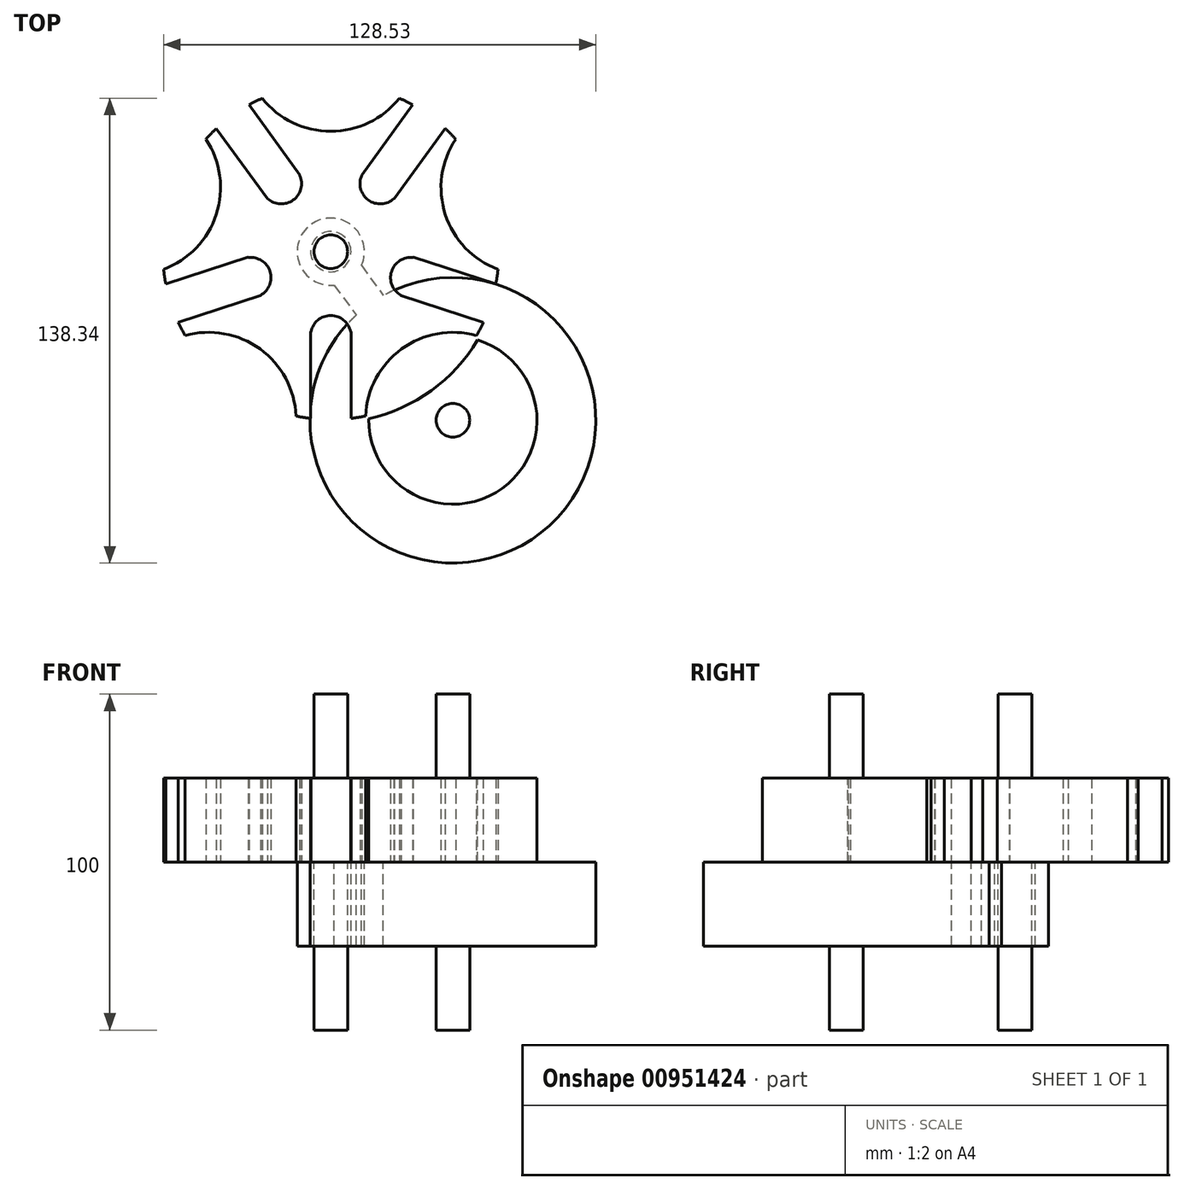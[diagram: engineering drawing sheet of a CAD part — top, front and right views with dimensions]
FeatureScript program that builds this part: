
annotation { "Feature Type Name" : "Feature", "Feature Type Description" : "" }
export const myFeature = defineFeature(function(context is Context, id is Id, definition is map)
    precondition{}
    {
        {
            var Q0;
            Q0=qCreatedBy(makeId("Top.planeOp"),FACE);
            var sketch = newSketch(context, id + "F0", { "sketchPlane" : qUnion([Q0])});
            skCircle(sketch, "E0", {"center": v(0, 0) * mm, "radius": 50 * mm});
            skCircle(sketch, "E1.cCircle", {"center": v(0, 0) * mm, "radius": 50 * mm, "construction": true});
            skLineSegment(sketch, "E1.0", {"start": v(0, -50) * mm, "end": v(-47.55, -15.45) * mm});
            skLineSegment(sketch, "E1.1", {"start": v(-47.55, -15.45) * mm, "end": v(-29.39, 40.45) * mm});
            skLineSegment(sketch, "E1.2", {"start": v(-29.39, 40.45) * mm, "end": v(29.39, 40.45) * mm});
            skLineSegment(sketch, "E1.3", {"start": v(29.39, 40.45) * mm, "end": v(47.55, -15.45) * mm});
            skLineSegment(sketch, "E1.4", {"start": v(47.55, -15.45) * mm, "end": v(0, -50) * mm});
            skLineSegment(sketch, "E2", {"start": v(-47.55, -15.45) * mm, "end": v(0, 0) * mm});
            skLineSegment(sketch, "E3", {"start": v(0, -50) * mm, "end": v(0, 0) * mm});
            skLineSegment(sketch, "E4", {"start": v(47.55, -15.45) * mm, "end": v(0, 0) * mm});
            skLineSegment(sketch, "E5", {"start": v(29.39, 40.45) * mm, "end": v(0, 0) * mm});
            skLineSegment(sketch, "E6", {"start": v(-29.39, 40.45) * mm, "end": v(0, 0) * mm});
            skLineSegment(sketch, "E7.0", {"start": v(-34.24, 36.92) * mm, "end": v(-4.85, -3.53) * mm});
            skLineSegment(sketch, "E8.0", {"start": v(-24.54, 43.98) * mm, "end": v(4.85, 3.53) * mm});
            skLineSegment(sketch, "E9.0", {"start": v(-45.7, -21.16) * mm, "end": v(1.85, -5.7) * mm});
            skLineSegment(sketch, "E10.0", {"start": v(-49.4, -9.74) * mm, "end": v(-1.85, 5.7) * mm});
            skLineSegment(sketch, "E11.0", {"start": v(-6, -50) * mm, "end": v(-6, 0) * mm});
            skLineSegment(sketch, "E12.0", {"start": v(6, -50) * mm, "end": v(6, 0) * mm});
            skLineSegment(sketch, "E13.0", {"start": v(49.4, -9.74) * mm, "end": v(1.85, 5.7) * mm});
            skLineSegment(sketch, "E14.0", {"start": v(45.7, -21.16) * mm, "end": v(-1.85, -5.7) * mm});
            skLineSegment(sketch, "E15.0", {"start": v(24.54, 43.98) * mm, "end": v(-4.85, 3.53) * mm});
            skLineSegment(sketch, "E16.0", {"start": v(34.24, 36.92) * mm, "end": v(4.85, -3.53) * mm});
            skLineSegment(sketch, "E17", {"start": v(-47.55, -15.45) * mm, "end": v(-36.33, -50) * mm});
            skLineSegment(sketch, "E18", {"start": v(0, -50) * mm, "end": v(-36.33, -50) * mm});
            skLineSegment(sketch, "E19", {"start": v(0, -50) * mm, "end": v(36.33, -50) * mm});
            skLineSegment(sketch, "E20", {"start": v(47.55, -15.45) * mm, "end": v(36.33, -50) * mm});
            skLineSegment(sketch, "E21", {"start": v(47.55, -15.45) * mm, "end": v(58.78, 19.1) * mm});
            skLineSegment(sketch, "E22", {"start": v(29.39, 40.45) * mm, "end": v(58.78, 19.1) * mm});
            skLineSegment(sketch, "E23", {"start": v(29.39, 40.45) * mm, "end": v(0, 61.8) * mm});
            skLineSegment(sketch, "E24", {"start": v(-29.39, 40.45) * mm, "end": v(0, 61.8) * mm});
            skLineSegment(sketch, "E25", {"start": v(-47.55, -15.45) * mm, "end": v(-58.78, 19.1) * mm});
            skLineSegment(sketch, "E26", {"start": v(-29.39, 40.45) * mm, "end": v(-58.78, 19.1) * mm});
            skCircle(sketch, "E27", {"center": v(36.33, -50) * mm, "radius": 36.33 * mm});
            skCircle(sketch, "E28", {"center": v(-36.33, -50) * mm, "radius": 36.33 * mm});
            skCircle(sketch, "E29", {"center": v(58.78, 19.1) * mm, "radius": 36.33 * mm});
            skCircle(sketch, "E30", {"center": v(0, 61.8) * mm, "radius": 36.33 * mm});
            skCircle(sketch, "E31", {"center": v(-58.78, 19.1) * mm, "radius": 36.33 * mm});
            skCircle(sketch, "E32", {"center": v(-6, -30) * mm, "radius": 6 * mm});
            skCircle(sketch, "E33", {"center": v(0, 0) * mm, "radius": 24.6 * mm});
            skCircle(sketch, "E34", {"center": v(0, -25) * mm, "radius": 6 * mm});
            skCircle(sketch, "E35", {"center": v(23.78, -7.73) * mm, "radius": 6 * mm});
            skCircle(sketch, "E36", {"center": v(14.7, 20.23) * mm, "radius": 6 * mm});
            skCircle(sketch, "E37", {"center": v(-14.7, 20.23) * mm, "radius": 6 * mm});
            skCircle(sketch, "E38", {"center": v(-23.78, -7.73) * mm, "radius": 6 * mm});
            skCircle(sketch, "E39", {"center": v(0, 0) * mm, "radius": 5 * mm});
            skCircle(sketch, "E40", {"center": v(36.33, -50) * mm, "radius": 26 * mm});
            skCircle(sketch, "E41", {"center": v(-36.33, -50) * mm, "radius": 26 * mm});
            skCircle(sketch, "E42", {"center": v(58.78, 19.1) * mm, "radius": 26 * mm});
            skCircle(sketch, "E43", {"center": v(0, 61.8) * mm, "radius": 26 * mm});
            skCircle(sketch, "E44", {"center": v(-58.78, 19.1) * mm, "radius": 26 * mm});
            skSolve(sketch);
        }
        {
            var Q0;
            {var subQ1=sQuery(id+"F0.wireOp",EDGE,"E1.2");var subQ7=sQuery(id+"F0.wireOp",EDGE,"E8.0");var subQ8=makeQuery(id+"F0.imprint","INTERSECT",VERTEX,{"derivedFrom":[subQ1,subQ7]});Q0=makeQuery(id+"F0.imprint","IMPRINT",FACE,{"disambiguationData":[TD([[makeQuery(id+"F0.imprint","IMPRINT",EDGE,{"disambiguationData":[TD([[subQ8,-1.0]])],"derivedFrom":subQ1}),-1.0]])]});}
            var Q1;
            {var subQ0=sQuery(id+"F0.wireOp",EDGE,"E15.0");var subQ1=sQuery(id+"F0.wireOp",EDGE,"E0");var subQ2=makeQuery(id+"F0.imprint","INTERSECT",VERTEX,{"derivedFrom":[subQ1,subQ0]});Q1=makeQuery(id+"F0.imprint","IMPRINT",FACE,{"disambiguationData":[TD([[makeQuery(id+"F0.imprint","IMPRINT",EDGE,{"disambiguationData":[TD([[subQ2,-1.0]])],"derivedFrom":subQ1}),1.0]])]});}
            var Q2;
            {var subQ0=sQuery(id+"F0.wireOp",EDGE,"E43");var subQ1=sQuery(id+"F0.wireOp",EDGE,"E0");var subQ2=makeQuery(id+"F0.imprint","INTERSECT",VERTEX,{"disambiguationData":[OD(1.0)],"derivedFrom":[subQ1,subQ0]});Q2=makeQuery(id+"F0.imprint","IMPRINT",FACE,{"disambiguationData":[TD([[makeQuery(id+"F0.imprint","IMPRINT",EDGE,{"disambiguationData":[TD([[subQ2,-1.0]])],"derivedFrom":subQ1}),1.0]])]});}
            var Q3;
            {var subQ4=sQuery(id+"F0.wireOp",EDGE,"E8.0");var subQ6=sQuery(id+"F0.wireOp",EDGE,"E30");var subQ9=makeQuery(id+"F0.imprint","INTERSECT",VERTEX,{"derivedFrom":[subQ4,subQ6]});Q3=makeQuery(id+"F0.imprint","IMPRINT",FACE,{"disambiguationData":[TD([[makeQuery(id+"F0.imprint","IMPRINT",EDGE,{"disambiguationData":[TD([[subQ9,-1.0]])],"derivedFrom":subQ4}),1.0]])]});}
            var Q4;
            {var subQ0=sQuery(id+"F0.wireOp",EDGE,"E33");var subQ1=sQuery(id+"F0.wireOp",EDGE,"E8.0");var subQ2=makeQuery(id+"F0.imprint","INTERSECT",VERTEX,{"derivedFrom":[subQ1,subQ0]});Q4=makeQuery(id+"F0.imprint","IMPRINT",FACE,{"disambiguationData":[TD([[makeQuery(id+"F0.imprint","IMPRINT",EDGE,{"disambiguationData":[TD([[subQ2,-1.0]])],"derivedFrom":subQ1}),1.0]])]});}
            var Q5;
            {var subQ3=sQuery(id+"F0.wireOp",EDGE,"E37");var subQ9=sQuery(id+"F0.wireOp",EDGE,"E6");var subQ10=makeQuery(id+"F0.imprint","INTERSECT",VERTEX,{"disambiguationData":[OD(1.0)],"derivedFrom":[subQ9,subQ3]});Q5=makeQuery(id+"F0.imprint","IMPRINT",FACE,{"disambiguationData":[TD([[makeQuery(id+"F0.imprint","IMPRINT",EDGE,{"disambiguationData":[TD([[subQ10,-1.0]])],"derivedFrom":subQ9}),1.0]])]});}
            var Q6;
            {var subQ3=sQuery(id+"F0.wireOp",EDGE,"E37");var subQ9=sQuery(id+"F0.wireOp",EDGE,"E6");var subQ10=makeQuery(id+"F0.imprint","INTERSECT",VERTEX,{"disambiguationData":[OD(1.0)],"derivedFrom":[subQ9,subQ3]});Q6=makeQuery(id+"F0.imprint","IMPRINT",FACE,{"disambiguationData":[TD([[makeQuery(id+"F0.imprint","IMPRINT",EDGE,{"disambiguationData":[TD([[subQ10,-1.0]])],"derivedFrom":subQ9}),-1.0]])]});}
            var Q7;
            {var subQ7=sQuery(id+"F0.wireOp",EDGE,"E36");var subQ9=sQuery(id+"F0.wireOp",EDGE,"E5");var subQ11=makeQuery(id+"F0.imprint","INTERSECT",VERTEX,{"disambiguationData":[OD(1.0)],"derivedFrom":[subQ9,subQ7]});Q7=makeQuery(id+"F0.imprint","IMPRINT",FACE,{"disambiguationData":[TD([[makeQuery(id+"F0.imprint","IMPRINT",EDGE,{"disambiguationData":[TD([[subQ11,-1.0]])],"derivedFrom":subQ9}),-1.0]])]});}
            var Q8;
            {var subQ3=sQuery(id+"F0.wireOp",EDGE,"E36");var subQ7=sQuery(id+"F0.wireOp",EDGE,"E5");var subQ8=makeQuery(id+"F0.imprint","INTERSECT",VERTEX,{"disambiguationData":[OD(1.0)],"derivedFrom":[subQ7,subQ3]});Q8=makeQuery(id+"F0.imprint","IMPRINT",FACE,{"disambiguationData":[TD([[makeQuery(id+"F0.imprint","IMPRINT",EDGE,{"disambiguationData":[TD([[subQ8,-1.0]])],"derivedFrom":subQ7}),1.0]])]});}
            var Q9;
            {var subQ0=sQuery(id+"F0.wireOp",EDGE,"E33");var subQ1=sQuery(id+"F0.wireOp",EDGE,"E13.0");var subQ2=makeQuery(id+"F0.imprint","INTERSECT",VERTEX,{"derivedFrom":[subQ1,subQ0]});Q9=makeQuery(id+"F0.imprint","IMPRINT",FACE,{"disambiguationData":[TD([[makeQuery(id+"F0.imprint","IMPRINT",EDGE,{"disambiguationData":[TD([[subQ2,-1.0]])],"derivedFrom":subQ1}),-1.0]])]});}
            var Q10;
            {var subQ3=sQuery(id+"F0.wireOp",EDGE,"E35");var subQ5=sQuery(id+"F0.wireOp",EDGE,"E4");var subQ6=makeQuery(id+"F0.imprint","INTERSECT",VERTEX,{"disambiguationData":[OD(1.0)],"derivedFrom":[subQ5,subQ3]});Q10=makeQuery(id+"F0.imprint","IMPRINT",FACE,{"disambiguationData":[TD([[makeQuery(id+"F0.imprint","IMPRINT",EDGE,{"disambiguationData":[TD([[subQ6,-1.0]])],"derivedFrom":subQ5}),-1.0]])]});}
            var Q11;
            {var subQ3=sQuery(id+"F0.wireOp",EDGE,"E35");var subQ9=sQuery(id+"F0.wireOp",EDGE,"E4");var subQ10=makeQuery(id+"F0.imprint","INTERSECT",VERTEX,{"disambiguationData":[OD(1.0)],"derivedFrom":[subQ9,subQ3]});Q11=makeQuery(id+"F0.imprint","IMPRINT",FACE,{"disambiguationData":[TD([[makeQuery(id+"F0.imprint","IMPRINT",EDGE,{"disambiguationData":[TD([[subQ10,-1.0]])],"derivedFrom":subQ9}),1.0]])]});}
            var Q12;
            {var subQ0=sQuery(id+"F0.wireOp",EDGE,"E33");var subQ1=sQuery(id+"F0.wireOp",EDGE,"E12.0");var subQ2=makeQuery(id+"F0.imprint","INTERSECT",VERTEX,{"derivedFrom":[subQ1,subQ0]});Q12=makeQuery(id+"F0.imprint","IMPRINT",FACE,{"disambiguationData":[TD([[makeQuery(id+"F0.imprint","IMPRINT",EDGE,{"disambiguationData":[TD([[subQ2,-1.0]])],"derivedFrom":subQ1}),-1.0]])]});}
            var Q13;
            {var subQ3=sQuery(id+"F0.wireOp",EDGE,"E34");var subQ8=sQuery(id+"F0.wireOp",EDGE,"E3");var subQ11=makeQuery(id+"F0.imprint","INTERSECT",VERTEX,{"disambiguationData":[OD(1.0)],"derivedFrom":[subQ8,subQ3]});Q13=makeQuery(id+"F0.imprint","IMPRINT",FACE,{"disambiguationData":[TD([[makeQuery(id+"F0.imprint","IMPRINT",EDGE,{"disambiguationData":[TD([[subQ11,-1.0]])],"derivedFrom":subQ8}),-1.0]])]});}
            var Q14;
            {var subQ3=sQuery(id+"F0.wireOp",EDGE,"E34");var subQ9=sQuery(id+"F0.wireOp",EDGE,"E3");var subQ10=makeQuery(id+"F0.imprint","INTERSECT",VERTEX,{"disambiguationData":[OD(1.0)],"derivedFrom":[subQ9,subQ3]});Q14=makeQuery(id+"F0.imprint","IMPRINT",FACE,{"disambiguationData":[TD([[makeQuery(id+"F0.imprint","IMPRINT",EDGE,{"disambiguationData":[TD([[subQ10,-1.0]])],"derivedFrom":subQ9}),1.0]])]});}
            var Q15;
            {var subQ0=sQuery(id+"F0.wireOp",EDGE,"E33");var subQ1=sQuery(id+"F0.wireOp",EDGE,"E9.0");var subQ2=makeQuery(id+"F0.imprint","INTERSECT",VERTEX,{"derivedFrom":[subQ1,subQ0]});Q15=makeQuery(id+"F0.imprint","IMPRINT",FACE,{"disambiguationData":[TD([[makeQuery(id+"F0.imprint","IMPRINT",EDGE,{"disambiguationData":[TD([[subQ2,-1.0]])],"derivedFrom":subQ1}),-1.0]])]});}
            var Q16;
            {var subQ7=sQuery(id+"F0.wireOp",EDGE,"E38");var subQ9=sQuery(id+"F0.wireOp",EDGE,"E2");var subQ10=makeQuery(id+"F0.imprint","INTERSECT",VERTEX,{"disambiguationData":[OD(1.0)],"derivedFrom":[subQ9,subQ7]});Q16=makeQuery(id+"F0.imprint","IMPRINT",FACE,{"disambiguationData":[TD([[makeQuery(id+"F0.imprint","IMPRINT",EDGE,{"disambiguationData":[TD([[subQ10,-1.0]])],"derivedFrom":subQ9}),-1.0]])]});}
            var Q17;
            {var subQ0=sQuery(id+"F0.wireOp",EDGE,"E33");var subQ1=sQuery(id+"F0.wireOp",EDGE,"E7.0");var subQ2=makeQuery(id+"F0.imprint","INTERSECT",VERTEX,{"derivedFrom":[subQ1,subQ0]});Q17=makeQuery(id+"F0.imprint","IMPRINT",FACE,{"disambiguationData":[TD([[makeQuery(id+"F0.imprint","IMPRINT",EDGE,{"disambiguationData":[TD([[subQ2,-1.0]])],"derivedFrom":subQ1}),-1.0]])]});}
            var Q18;
            {var subQ3=sQuery(id+"F0.wireOp",EDGE,"E38");var subQ6=sQuery(id+"F0.wireOp",EDGE,"E2");var subQ11=makeQuery(id+"F0.imprint","INTERSECT",VERTEX,{"disambiguationData":[OD(1.0)],"derivedFrom":[subQ6,subQ3]});Q18=makeQuery(id+"F0.imprint","IMPRINT",FACE,{"disambiguationData":[TD([[makeQuery(id+"F0.imprint","IMPRINT",EDGE,{"disambiguationData":[TD([[subQ11,-1.0]])],"derivedFrom":subQ6}),1.0]])]});}
            var Q19;
            {var subQ0=sQuery(id+"F0.wireOp",EDGE,"E16.0");var subQ1=sQuery(id+"F0.wireOp",EDGE,"E0");var subQ2=makeQuery(id+"F0.imprint","INTERSECT",VERTEX,{"derivedFrom":[subQ1,subQ0]});Q19=makeQuery(id+"F0.imprint","IMPRINT",FACE,{"disambiguationData":[TD([[makeQuery(id+"F0.imprint","IMPRINT",EDGE,{"disambiguationData":[TD([[subQ2,1.0]])],"derivedFrom":subQ1}),1.0]])]});}
            var Q20;
            {var subQ0=sQuery(id+"F0.wireOp",EDGE,"E16.0");var subQ1=sQuery(id+"F0.wireOp",EDGE,"E1.3");var subQ2=makeQuery(id+"F0.imprint","INTERSECT",VERTEX,{"derivedFrom":[subQ1,subQ0]});Q20=makeQuery(id+"F0.imprint","IMPRINT",FACE,{"disambiguationData":[TD([[makeQuery(id+"F0.imprint","IMPRINT",EDGE,{"disambiguationData":[TD([[subQ2,-1.0]])],"derivedFrom":subQ1}),-1.0]])]});}
            var Q21;
            {var subQ0=sQuery(id+"F0.wireOp",EDGE,"E29");var subQ4=sQuery(id+"F0.wireOp",EDGE,"E13.0");var subQ9=makeQuery(id+"F0.imprint","INTERSECT",VERTEX,{"derivedFrom":[subQ4,subQ0]});Q21=makeQuery(id+"F0.imprint","IMPRINT",FACE,{"disambiguationData":[TD([[makeQuery(id+"F0.imprint","IMPRINT",EDGE,{"disambiguationData":[TD([[subQ9,-1.0]])],"derivedFrom":subQ4}),-1.0]])]});}
            var Q22;
            {var subQ0=sQuery(id+"F0.wireOp",EDGE,"E13.0");var subQ1=sQuery(id+"F0.wireOp",EDGE,"E0");var subQ2=makeQuery(id+"F0.imprint","INTERSECT",VERTEX,{"derivedFrom":[subQ1,subQ0]});Q22=makeQuery(id+"F0.imprint","IMPRINT",FACE,{"disambiguationData":[TD([[makeQuery(id+"F0.imprint","IMPRINT",EDGE,{"disambiguationData":[TD([[subQ2,-1.0]])],"derivedFrom":subQ1}),1.0]])]});}
            var Q23;
            {var subQ4=sQuery(id+"F0.wireOp",EDGE,"E27");var subQ6=sQuery(id+"F0.wireOp",EDGE,"E12.0");var subQ9=makeQuery(id+"F0.imprint","INTERSECT",VERTEX,{"derivedFrom":[subQ6,subQ4]});Q23=makeQuery(id+"F0.imprint","IMPRINT",FACE,{"disambiguationData":[TD([[makeQuery(id+"F0.imprint","IMPRINT",EDGE,{"disambiguationData":[TD([[subQ9,-1.0]])],"derivedFrom":subQ6}),-1.0]])]});}
            var Q24;
            {var subQ1=sQuery(id+"F0.wireOp",EDGE,"E1.4");var subQ7=sQuery(id+"F0.wireOp",EDGE,"E14.0");var subQ8=makeQuery(id+"F0.imprint","INTERSECT",VERTEX,{"derivedFrom":[subQ1,subQ7]});Q24=makeQuery(id+"F0.imprint","IMPRINT",FACE,{"disambiguationData":[TD([[makeQuery(id+"F0.imprint","IMPRINT",EDGE,{"disambiguationData":[TD([[subQ8,-1.0]])],"derivedFrom":subQ1}),-1.0]])]});}
            var Q25;
            {var subQ0=sQuery(id+"F0.wireOp",EDGE,"E40");var subQ1=sQuery(id+"F0.wireOp",EDGE,"E0");var subQ2=makeQuery(id+"F0.imprint","INTERSECT",VERTEX,{"disambiguationData":[OD(1.0)],"derivedFrom":[subQ1,subQ0]});Q25=makeQuery(id+"F0.imprint","IMPRINT",FACE,{"disambiguationData":[TD([[makeQuery(id+"F0.imprint","IMPRINT",EDGE,{"disambiguationData":[TD([[subQ2,-1.0]])],"derivedFrom":subQ1}),1.0]])]});}
            var Q26;
            {var subQ0=sQuery(id+"F0.wireOp",EDGE,"E12.0");var subQ1=sQuery(id+"F0.wireOp",EDGE,"E0");var subQ2=makeQuery(id+"F0.imprint","INTERSECT",VERTEX,{"derivedFrom":[subQ1,subQ0]});Q26=makeQuery(id+"F0.imprint","IMPRINT",FACE,{"disambiguationData":[TD([[makeQuery(id+"F0.imprint","IMPRINT",EDGE,{"disambiguationData":[TD([[subQ2,-1.0]])],"derivedFrom":subQ1}),1.0]])]});}
            var Q27;
            {var subQ0=sQuery(id+"F0.wireOp",EDGE,"E28");var subQ1=sQuery(id+"F0.wireOp",EDGE,"E11.0");var subQ2=makeQuery(id+"F0.imprint","INTERSECT",VERTEX,{"derivedFrom":[subQ1,subQ0]});Q27=makeQuery(id+"F0.imprint","IMPRINT",FACE,{"disambiguationData":[TD([[makeQuery(id+"F0.imprint","IMPRINT",EDGE,{"disambiguationData":[TD([[subQ2,-1.0]])],"derivedFrom":subQ1}),1.0]])]});}
            var Q28;
            {var subQ0=sQuery(id+"F0.wireOp",EDGE,"E32");var subQ1=sQuery(id+"F0.wireOp",EDGE,"E11.0");var subQ2=makeQuery(id+"F0.imprint","INTERSECT",VERTEX,{"disambiguationData":[OD(0.0)],"derivedFrom":[subQ1,subQ0]});Q28=makeQuery(id+"F0.imprint","IMPRINT",FACE,{"disambiguationData":[TD([[makeQuery(id+"F0.imprint","IMPRINT",EDGE,{"disambiguationData":[TD([[subQ2,-1.0]])],"derivedFrom":subQ1}),1.0]])]});}
            var Q29;
            {var subQ5=sQuery(id+"F0.wireOp",EDGE,"E28");var subQ6=sQuery(id+"F0.wireOp",EDGE,"E9.0");var subQ7=makeQuery(id+"F0.imprint","INTERSECT",VERTEX,{"derivedFrom":[subQ6,subQ5]});Q29=makeQuery(id+"F0.imprint","IMPRINT",FACE,{"disambiguationData":[TD([[makeQuery(id+"F0.imprint","IMPRINT",EDGE,{"disambiguationData":[TD([[subQ7,-1.0]])],"derivedFrom":subQ6}),-1.0]])]});}
            var Q30;
            {var subQ0=sQuery(id+"F0.wireOp",EDGE,"E11.0");var subQ1=sQuery(id+"F0.wireOp",EDGE,"E1.0");var subQ2=makeQuery(id+"F0.imprint","INTERSECT",VERTEX,{"derivedFrom":[subQ1,subQ0]});Q30=makeQuery(id+"F0.imprint","IMPRINT",FACE,{"disambiguationData":[TD([[makeQuery(id+"F0.imprint","IMPRINT",EDGE,{"disambiguationData":[TD([[subQ2,-1.0]])],"derivedFrom":subQ1}),-1.0]])]});}
            var Q31;
            {var subQ0=sQuery(id+"F0.wireOp",EDGE,"E41");var subQ1=sQuery(id+"F0.wireOp",EDGE,"E0");var subQ2=makeQuery(id+"F0.imprint","INTERSECT",VERTEX,{"disambiguationData":[OD(1.0)],"derivedFrom":[subQ1,subQ0]});Q31=makeQuery(id+"F0.imprint","IMPRINT",FACE,{"disambiguationData":[TD([[makeQuery(id+"F0.imprint","IMPRINT",EDGE,{"disambiguationData":[TD([[subQ2,-1.0]])],"derivedFrom":subQ1}),1.0]])]});}
            var Q32;
            {var subQ0=sQuery(id+"F0.wireOp",EDGE,"E9.0");var subQ1=sQuery(id+"F0.wireOp",EDGE,"E0");var subQ2=makeQuery(id+"F0.imprint","INTERSECT",VERTEX,{"derivedFrom":[subQ1,subQ0]});Q32=makeQuery(id+"F0.imprint","IMPRINT",FACE,{"disambiguationData":[TD([[makeQuery(id+"F0.imprint","IMPRINT",EDGE,{"disambiguationData":[TD([[subQ2,-1.0]])],"derivedFrom":subQ1}),1.0]])]});}
            var Q33;
            {var subQ0=sQuery(id+"F0.wireOp",EDGE,"E44");var subQ1=sQuery(id+"F0.wireOp",EDGE,"E0");var subQ2=makeQuery(id+"F0.imprint","INTERSECT",VERTEX,{"disambiguationData":[OD(1.0)],"derivedFrom":[subQ1,subQ0]});Q33=makeQuery(id+"F0.imprint","IMPRINT",FACE,{"disambiguationData":[TD([[makeQuery(id+"F0.imprint","IMPRINT",EDGE,{"disambiguationData":[TD([[subQ2,-1.0]])],"derivedFrom":subQ1}),1.0]])]});}
            var Q34;
            {var subQ0=sQuery(id+"F0.wireOp",EDGE,"E10.0");var subQ1=sQuery(id+"F0.wireOp",EDGE,"E1.1");var subQ2=makeQuery(id+"F0.imprint","INTERSECT",VERTEX,{"derivedFrom":[subQ1,subQ0]});Q34=makeQuery(id+"F0.imprint","IMPRINT",FACE,{"disambiguationData":[TD([[makeQuery(id+"F0.imprint","IMPRINT",EDGE,{"disambiguationData":[TD([[subQ2,-1.0]])],"derivedFrom":subQ1}),-1.0]])]});}
            var Q35;
            {var subQ0=sQuery(id+"F0.wireOp",EDGE,"E31");var subQ4=sQuery(id+"F0.wireOp",EDGE,"E7.0");var subQ9=makeQuery(id+"F0.imprint","INTERSECT",VERTEX,{"derivedFrom":[subQ4,subQ0]});Q35=makeQuery(id+"F0.imprint","IMPRINT",FACE,{"disambiguationData":[TD([[makeQuery(id+"F0.imprint","IMPRINT",EDGE,{"disambiguationData":[TD([[subQ9,-1.0]])],"derivedFrom":subQ4}),-1.0]])]});}
            var Q36;
            {var subQ0=sQuery(id+"F0.wireOp",EDGE,"E7.0");var subQ1=sQuery(id+"F0.wireOp",EDGE,"E0");var subQ2=makeQuery(id+"F0.imprint","INTERSECT",VERTEX,{"derivedFrom":[subQ1,subQ0]});Q36=makeQuery(id+"F0.imprint","IMPRINT",FACE,{"disambiguationData":[TD([[makeQuery(id+"F0.imprint","IMPRINT",EDGE,{"disambiguationData":[TD([[subQ2,-1.0]])],"derivedFrom":subQ1}),1.0]])]});}
            var Q37;
            {var subQ1=sQuery(id+"F0.wireOp",EDGE,"E3");var subQ5=sQuery(id+"F0.wireOp",EDGE,"E39");var subQ6=makeQuery(id+"F0.imprint","INTERSECT",VERTEX,{"derivedFrom":[subQ1,subQ5]});Q37=makeQuery(id+"F0.imprint","IMPRINT",FACE,{"disambiguationData":[TD([[makeQuery(id+"F0.imprint","IMPRINT",EDGE,{"disambiguationData":[TD([[subQ6,-1.0]])],"derivedFrom":subQ5}),-1.0]])]});}
            var Q38;
            {var subQ5=sQuery(id+"F0.wireOp",EDGE,"E39");var subQ7=sQuery(id+"F0.wireOp",EDGE,"E4");var subQ9=makeQuery(id+"F0.imprint","INTERSECT",VERTEX,{"derivedFrom":[subQ7,subQ5]});Q38=makeQuery(id+"F0.imprint","IMPRINT",FACE,{"disambiguationData":[TD([[makeQuery(id+"F0.imprint","IMPRINT",EDGE,{"disambiguationData":[TD([[subQ9,-1.0]])],"derivedFrom":subQ5}),-1.0]])]});}
            var Q39;
            {var subQ5=sQuery(id+"F0.wireOp",EDGE,"E39");var subQ7=sQuery(id+"F0.wireOp",EDGE,"E5");var subQ9=makeQuery(id+"F0.imprint","INTERSECT",VERTEX,{"derivedFrom":[subQ7,subQ5]});Q39=makeQuery(id+"F0.imprint","IMPRINT",FACE,{"disambiguationData":[TD([[makeQuery(id+"F0.imprint","IMPRINT",EDGE,{"disambiguationData":[TD([[subQ9,-1.0]])],"derivedFrom":subQ5}),-1.0]])]});}
            var Q40;
            {var subQ1=sQuery(id+"F0.wireOp",EDGE,"E2");var subQ7=sQuery(id+"F0.wireOp",EDGE,"E39");var subQ9=makeQuery(id+"F0.imprint","INTERSECT",VERTEX,{"derivedFrom":[subQ1,subQ7]});Q40=makeQuery(id+"F0.imprint","IMPRINT",FACE,{"disambiguationData":[TD([[makeQuery(id+"F0.imprint","IMPRINT",EDGE,{"disambiguationData":[TD([[subQ9,-1.0]])],"derivedFrom":subQ7}),-1.0]])]});}
            var Q41;
            {var subQ5=sQuery(id+"F0.wireOp",EDGE,"E39");var subQ6=sQuery(id+"F0.wireOp",EDGE,"E2");var subQ7=makeQuery(id+"F0.imprint","INTERSECT",VERTEX,{"derivedFrom":[subQ6,subQ5]});Q41=makeQuery(id+"F0.imprint","IMPRINT",FACE,{"disambiguationData":[TD([[makeQuery(id+"F0.imprint","IMPRINT",EDGE,{"disambiguationData":[TD([[subQ7,1.0]])],"derivedFrom":subQ5}),-1.0]])]});}
            extrude(context, id + "F1", {"entities" : qUnion([Q0, Q1, Q2, Q3, Q4, Q5, Q6, Q7, Q8, Q9, Q10, Q11, Q12, Q13, Q14, Q15, Q16, Q17, Q18, Q19, Q20, Q21, Q22, Q23, Q24, Q25, Q26, Q27, Q28, Q29, Q30, Q31, Q32, Q33, Q34, Q35, Q36, Q37, Q38, Q39, Q40, Q41]), "depth" : 25 * mm, "offsetDistance" : 25 * mm});
        }
        {
            var Q0;
            {var subQ0=sQuery(id+"F0.wireOp",EDGE,"E39");var subQ1=sQuery(id+"F0.wireOp",EDGE,"E6");var subQ2=makeQuery(id+"F0.imprint","INTERSECT",VERTEX,{"derivedFrom":[subQ1,subQ0]});Q0=makeQuery(id+"F0.imprint","IMPRINT",FACE,{"disambiguationData":[TD([[makeQuery(id+"F0.imprint","IMPRINT",EDGE,{"disambiguationData":[TD([[subQ2,1.0]])],"derivedFrom":subQ0}),1.0]])]});}
            var Q1;
            {var subQ3=sQuery(id+"F0.wireOp",EDGE,"E39");var subQ5=sQuery(id+"F0.wireOp",EDGE,"E7.0");var subQ6=makeQuery(id+"F0.imprint","INTERSECT",VERTEX,{"derivedFrom":[subQ5,subQ3]});Q1=makeQuery(id+"F0.imprint","IMPRINT",FACE,{"disambiguationData":[TD([[makeQuery(id+"F0.imprint","IMPRINT",EDGE,{"disambiguationData":[TD([[subQ6,1.0]])],"derivedFrom":subQ3}),1.0]])]});}
            var Q2;
            {var subQ0=sQuery(id+"F0.wireOp",EDGE,"E39");var subQ1=sQuery(id+"F0.wireOp",EDGE,"E6");var subQ2=makeQuery(id+"F0.imprint","INTERSECT",VERTEX,{"derivedFrom":[subQ1,subQ0]});Q2=makeQuery(id+"F0.imprint","IMPRINT",FACE,{"disambiguationData":[TD([[makeQuery(id+"F0.imprint","IMPRINT",EDGE,{"disambiguationData":[TD([[subQ2,-1.0]])],"derivedFrom":subQ0}),1.0]])]});}
            var Q3;
            {var subQ0=sQuery(id+"F0.wireOp",EDGE,"E39");var subQ1=sQuery(id+"F0.wireOp",EDGE,"E3");var subQ2=makeQuery(id+"F0.imprint","INTERSECT",VERTEX,{"derivedFrom":[subQ1,subQ0]});Q3=makeQuery(id+"F0.imprint","IMPRINT",FACE,{"disambiguationData":[TD([[makeQuery(id+"F0.imprint","IMPRINT",EDGE,{"disambiguationData":[TD([[subQ2,-1.0]])],"derivedFrom":subQ0}),1.0]])]});}
            var Q4;
            {var subQ0=sQuery(id+"F0.wireOp",EDGE,"E39");var subQ1=sQuery(id+"F0.wireOp",EDGE,"E4");var subQ2=makeQuery(id+"F0.imprint","INTERSECT",VERTEX,{"derivedFrom":[subQ1,subQ0]});Q4=makeQuery(id+"F0.imprint","IMPRINT",FACE,{"disambiguationData":[TD([[makeQuery(id+"F0.imprint","IMPRINT",EDGE,{"disambiguationData":[TD([[subQ2,-1.0]])],"derivedFrom":subQ0}),1.0]])]});}
            var Q5;
            {var subQ0=sQuery(id+"F0.wireOp",EDGE,"E39");var subQ1=sQuery(id+"F0.wireOp",EDGE,"E3");var subQ2=makeQuery(id+"F0.imprint","INTERSECT",VERTEX,{"derivedFrom":[subQ1,subQ0]});Q5=makeQuery(id+"F0.imprint","IMPRINT",FACE,{"disambiguationData":[TD([[makeQuery(id+"F0.imprint","IMPRINT",EDGE,{"disambiguationData":[TD([[subQ2,1.0]])],"derivedFrom":subQ0}),1.0]])]});}
            var Q6;
            {var subQ3=sQuery(id+"F0.wireOp",EDGE,"E39");var subQ5=sQuery(id+"F0.wireOp",EDGE,"E12.0");var subQ8=makeQuery(id+"F0.imprint","INTERSECT",VERTEX,{"derivedFrom":[subQ5,subQ3]});Q6=makeQuery(id+"F0.imprint","IMPRINT",FACE,{"disambiguationData":[TD([[makeQuery(id+"F0.imprint","IMPRINT",EDGE,{"disambiguationData":[TD([[subQ8,1.0]])],"derivedFrom":subQ3}),1.0]])]});}
            var Q7;
            {var subQ3=sQuery(id+"F0.wireOp",EDGE,"E39");var subQ7=sQuery(id+"F0.wireOp",EDGE,"E13.0");var subQ9=makeQuery(id+"F0.imprint","INTERSECT",VERTEX,{"derivedFrom":[subQ7,subQ3]});Q7=makeQuery(id+"F0.imprint","IMPRINT",FACE,{"disambiguationData":[TD([[makeQuery(id+"F0.imprint","IMPRINT",EDGE,{"disambiguationData":[TD([[subQ9,1.0]])],"derivedFrom":subQ3}),1.0]])]});}
            var Q8;
            {var subQ0=sQuery(id+"F0.wireOp",EDGE,"E39");var subQ1=sQuery(id+"F0.wireOp",EDGE,"E5");var subQ2=makeQuery(id+"F0.imprint","INTERSECT",VERTEX,{"derivedFrom":[subQ1,subQ0]});Q8=makeQuery(id+"F0.imprint","IMPRINT",FACE,{"disambiguationData":[TD([[makeQuery(id+"F0.imprint","IMPRINT",EDGE,{"disambiguationData":[TD([[subQ2,1.0]])],"derivedFrom":subQ0}),1.0]])]});}
            var Q9;
            {var subQ0=sQuery(id+"F0.wireOp",EDGE,"E39");var subQ1=sQuery(id+"F0.wireOp",EDGE,"E2");var subQ2=makeQuery(id+"F0.imprint","INTERSECT",VERTEX,{"derivedFrom":[subQ1,subQ0]});Q9=makeQuery(id+"F0.imprint","IMPRINT",FACE,{"disambiguationData":[TD([[makeQuery(id+"F0.imprint","IMPRINT",EDGE,{"disambiguationData":[TD([[subQ2,1.0]])],"derivedFrom":subQ0}),1.0]])]});}
            var Q10;
            {var subQ0=sQuery(id+"F0.wireOp",EDGE,"E39");var subQ1=sQuery(id+"F0.wireOp",EDGE,"E2");var subQ2=makeQuery(id+"F0.imprint","INTERSECT",VERTEX,{"derivedFrom":[subQ1,subQ0]});Q10=makeQuery(id+"F0.imprint","IMPRINT",FACE,{"disambiguationData":[TD([[makeQuery(id+"F0.imprint","IMPRINT",EDGE,{"disambiguationData":[TD([[subQ2,-1.0]])],"derivedFrom":subQ0}),1.0]])]});}
            var Q11;
            {var subQ0=sQuery(id+"F0.wireOp",EDGE,"E8.0");var subQ3=sQuery(id+"F0.wireOp",EDGE,"E39");var subQ4=makeQuery(id+"F0.imprint","INTERSECT",VERTEX,{"derivedFrom":[subQ0,subQ3]});Q11=makeQuery(id+"F0.imprint","IMPRINT",FACE,{"disambiguationData":[TD([[makeQuery(id+"F0.imprint","IMPRINT",EDGE,{"disambiguationData":[TD([[subQ4,-1.0]])],"derivedFrom":subQ3}),1.0]])]});}
            var Q12;
            {var subQ0=sQuery(id+"F0.wireOp",EDGE,"E39");var subQ1=sQuery(id+"F0.wireOp",EDGE,"E5");var subQ2=makeQuery(id+"F0.imprint","INTERSECT",VERTEX,{"derivedFrom":[subQ1,subQ0]});Q12=makeQuery(id+"F0.imprint","IMPRINT",FACE,{"disambiguationData":[TD([[makeQuery(id+"F0.imprint","IMPRINT",EDGE,{"disambiguationData":[TD([[subQ2,-1.0]])],"derivedFrom":subQ0}),1.0]])]});}
            var Q13;
            {var subQ0=sQuery(id+"F0.wireOp",EDGE,"E39");var subQ1=sQuery(id+"F0.wireOp",EDGE,"E4");var subQ2=makeQuery(id+"F0.imprint","INTERSECT",VERTEX,{"derivedFrom":[subQ1,subQ0]});Q13=makeQuery(id+"F0.imprint","IMPRINT",FACE,{"disambiguationData":[TD([[makeQuery(id+"F0.imprint","IMPRINT",EDGE,{"disambiguationData":[TD([[subQ2,1.0]])],"derivedFrom":subQ0}),1.0]])]});}
            var Q14;
            {var subQ0=sQuery(id+"F0.wireOp",EDGE,"E9.0");var subQ3=sQuery(id+"F0.wireOp",EDGE,"E39");var subQ4=makeQuery(id+"F0.imprint","INTERSECT",VERTEX,{"derivedFrom":[subQ0,subQ3]});Q14=makeQuery(id+"F0.imprint","IMPRINT",FACE,{"disambiguationData":[TD([[makeQuery(id+"F0.imprint","IMPRINT",EDGE,{"disambiguationData":[TD([[subQ4,1.0]])],"derivedFrom":subQ3}),1.0]])]});}
            extrude(context, id + "F2", {"entities" : qUnion([Q0, Q1, Q2, Q3, Q4, Q5, Q6, Q7, Q8, Q9, Q10, Q11, Q12, Q13, Q14]), "operationType" : NewBodyOperationType.ADD, "oppositeDirection" : true, "depth" : 50 * mm, "offsetDistance" : 25 * mm, "hasSecondDirection" : true, "secondDirectionOppositeDirection" : false, "secondDirectionDepth" : 50 * mm});
        }
        {
            var Q0;
            Q0=qCreatedBy(makeId("Top.planeOp"),FACE);
            var sketch = newSketch(context, id + "F3", { "sketchPlane" : qUnion([Q0])});
            skCircle(sketch, "E45", {"center": v(36.31, -50.18) * mm, "radius": 5 * mm});
            skCircle(sketch, "E46", {"center": v(36.31, -50.18) * mm, "radius": 25 * mm});
            skCircle(sketch, "E47", {"center": v(36.31, -50.18) * mm, "radius": 42.5 * mm});
            skCircle(sketch, "E48", {"center": v(0, 0) * mm, "radius": 51 * mm});
            skLineSegment(sketch, "E49", {"start": v(0, 0) * mm, "end": v(36.31, -50.18) * mm});
            skCircle(sketch, "E50", {"center": v(14.96, -20.67) * mm, "radius": 6 * mm});
            skSolve(sketch);
        }
        {
            var Q0;
            Q0=makeQuery(id+"F3.imprint","IMPRINT",FACE,{"disambiguationData":[TD([[makeQuery(id+"F3.imprint","IMPRINT",EDGE,{"derivedFrom":sQuery(id+"F3.wireOp",EDGE,"E45")}),-1.0]])]});
            extrude(context, id + "F4", {"entities" : qUnion([Q0]), "oppositeDirection" : true, "depth" : 25 * mm, "offsetDistance" : 25 * mm, "hasSecondDirection" : true, "secondDirectionOppositeDirection" : false, "secondDirectionDepth" : 25 * mm});
        }
        {
            var Q0;
            {var subQ0=sQuery(id+"F0.wireOp",EDGE,"E42");var subQ1=sQuery(id+"F0.wireOp",EDGE,"E1.3");var subQ2=makeQuery(id+"F0.imprint","INTERSECT",VERTEX,{"disambiguationData":[OD(0.0)],"derivedFrom":[subQ1,subQ0]});Q0=makeQuery(id+"F0.imprint","IMPRINT",FACE,{"disambiguationData":[TD([[makeQuery(id+"F0.imprint","IMPRINT",EDGE,{"disambiguationData":[TD([[subQ2,-1.0]])],"derivedFrom":subQ1}),-1.0]])]});}
            var sketch = newSketch(context, id + "F5", { "sketchPlane" : qUnion([Q0])});
            skCircle(sketch, "E51", {"center": v(0, 0) * mm, "radius": 6 * mm});
            skCircle(sketch, "E52", {"center": v(36.18, -49.9) * mm, "radius": 6 * mm});
            skCircle(sketch, "E53", {"center": v(36.18, -49.9) * mm, "radius": 10 * mm});
            skCircle(sketch, "E54", {"center": v(0, 0) * mm, "radius": 10 * mm});
            skLineSegment(sketch, "E55", {"start": v(0, 0) * mm, "end": v(36.18, -49.9) * mm});
            skLineSegment(sketch, "E56.0", {"start": v(-4.05, -2.93) * mm, "end": v(32.13, -52.84) * mm});
            skLineSegment(sketch, "E57.0", {"start": v(4.05, 2.93) * mm, "end": v(40.23, -46.97) * mm});
            skSolve(sketch);
        }
        {
            var Q0;
            {var subQ0=sQuery(id+"F5.wireOp",EDGE,"E57.0");var subQ1=sQuery(id+"F5.wireOp",EDGE,"E52");var subQ2=makeQuery(id+"F5.imprint","INTERSECT",VERTEX,{"derivedFrom":[subQ1,subQ0]});Q0=makeQuery(id+"F5.imprint","IMPRINT",FACE,{"disambiguationData":[TD([[makeQuery(id+"F5.imprint","IMPRINT",EDGE,{"disambiguationData":[TD([[subQ2,1.0]])],"derivedFrom":subQ1}),-1.0]])]});}
            var Q1;
            {var subQ0=sQuery(id+"F5.wireOp",EDGE,"E56.0");var subQ1=sQuery(id+"F5.wireOp",EDGE,"E51");var subQ2=makeQuery(id+"F5.imprint","INTERSECT",VERTEX,{"derivedFrom":[subQ1,subQ0]});Q1=makeQuery(id+"F5.imprint","IMPRINT",FACE,{"disambiguationData":[TD([[makeQuery(id+"F5.imprint","IMPRINT",EDGE,{"disambiguationData":[TD([[subQ2,1.0]])],"derivedFrom":subQ1}),-1.0]])]});}
            var Q2;
            {var subQ0=sQuery(id+"F5.wireOp",EDGE,"E55");var subQ1=sQuery(id+"F5.wireOp",EDGE,"E52");var subQ2=makeQuery(id+"F5.imprint","INTERSECT",VERTEX,{"derivedFrom":[subQ1,subQ0]});Q2=makeQuery(id+"F5.imprint","IMPRINT",FACE,{"disambiguationData":[TD([[makeQuery(id+"F5.imprint","IMPRINT",EDGE,{"disambiguationData":[TD([[subQ2,-1.0]])],"derivedFrom":subQ1}),-1.0]])]});}
            var Q3;
            {var subQ0=sQuery(id+"F5.wireOp",EDGE,"E55");var subQ1=sQuery(id+"F5.wireOp",EDGE,"E52");var subQ2=makeQuery(id+"F5.imprint","INTERSECT",VERTEX,{"derivedFrom":[subQ1,subQ0]});Q3=makeQuery(id+"F5.imprint","IMPRINT",FACE,{"disambiguationData":[TD([[makeQuery(id+"F5.imprint","IMPRINT",EDGE,{"disambiguationData":[TD([[subQ2,1.0]])],"derivedFrom":subQ1}),-1.0]])]});}
            var Q4;
            {var subQ0=sQuery(id+"F5.wireOp",EDGE,"E57.0");var subQ1=sQuery(id+"F5.wireOp",EDGE,"E51");var subQ2=makeQuery(id+"F5.imprint","INTERSECT",VERTEX,{"derivedFrom":[subQ1,subQ0]});Q4=makeQuery(id+"F5.imprint","IMPRINT",FACE,{"disambiguationData":[TD([[makeQuery(id+"F5.imprint","IMPRINT",EDGE,{"disambiguationData":[TD([[subQ2,1.0]])],"derivedFrom":subQ1}),-1.0]])]});}
            var Q5;
            {var subQ0=sQuery(id+"F5.wireOp",EDGE,"E57.0");var subQ1=sQuery(id+"F5.wireOp",EDGE,"E53");var subQ2=makeQuery(id+"F5.imprint","INTERSECT",VERTEX,{"derivedFrom":[subQ1,subQ0]});Q5=makeQuery(id+"F5.imprint","IMPRINT",FACE,{"disambiguationData":[TD([[makeQuery(id+"F5.imprint","IMPRINT",EDGE,{"disambiguationData":[TD([[subQ2,-1.0]])],"derivedFrom":subQ1}),-1.0]])]});}
            var Q6;
            {var subQ0=sQuery(id+"F5.wireOp",EDGE,"E56.0");var subQ1=sQuery(id+"F5.wireOp",EDGE,"E53");var subQ2=makeQuery(id+"F5.imprint","INTERSECT",VERTEX,{"derivedFrom":[subQ1,subQ0]});Q6=makeQuery(id+"F5.imprint","IMPRINT",FACE,{"disambiguationData":[TD([[makeQuery(id+"F5.imprint","IMPRINT",EDGE,{"disambiguationData":[TD([[subQ2,1.0]])],"derivedFrom":subQ1}),-1.0]])]});}
            var Q7;
            {var subQ0=sQuery(id+"F5.wireOp",EDGE,"E56.0");var subQ1=sQuery(id+"F5.wireOp",EDGE,"E51");var subQ2=makeQuery(id+"F5.imprint","INTERSECT",VERTEX,{"derivedFrom":[subQ1,subQ0]});Q7=makeQuery(id+"F5.imprint","IMPRINT",FACE,{"disambiguationData":[TD([[makeQuery(id+"F5.imprint","IMPRINT",EDGE,{"disambiguationData":[TD([[subQ2,-1.0]])],"derivedFrom":subQ1}),-1.0]])]});}
            extrude(context, id + "F6", {"entities" : qUnion([Q0, Q1, Q2, Q3, Q4, Q5, Q6, Q7]), "oppositeDirection" : true, "depth" : 25 * mm, "offsetDistance" : 25 * mm});
        }
        {
            var Q0;
            {var subQ0=sQuery(id+"F3.wireOp",EDGE,"E49");var subQ1=sQuery(id+"F3.wireOp",EDGE,"E46");var subQ2=makeQuery(id+"F3.imprint","INTERSECT",VERTEX,{"derivedFrom":[subQ1,subQ0]});Q0=makeQuery(id+"F3.imprint","IMPRINT",FACE,{"disambiguationData":[TD([[makeQuery(id+"F3.imprint","IMPRINT",EDGE,{"disambiguationData":[TD([[subQ2,1.0]])],"derivedFrom":subQ1}),1.0]])]});}
            var Q1;
            {var subQ0=sQuery(id+"F3.wireOp",EDGE,"E49");var subQ8=sQuery(id+"F3.wireOp",EDGE,"E46");var subQ10=makeQuery(id+"F3.imprint","INTERSECT",VERTEX,{"derivedFrom":[subQ8,subQ0]});Q1=makeQuery(id+"F3.imprint","IMPRINT",FACE,{"disambiguationData":[TD([[makeQuery(id+"F3.imprint","IMPRINT",EDGE,{"disambiguationData":[TD([[subQ10,-1.0]])],"derivedFrom":subQ8}),-1.0]])]});}
            var Q2;
            {var subQ0=sQuery(id+"F3.wireOp",EDGE,"E49");var subQ5=sQuery(id+"F3.wireOp",EDGE,"E46");var subQ6=makeQuery(id+"F3.imprint","INTERSECT",VERTEX,{"derivedFrom":[subQ5,subQ0]});Q2=makeQuery(id+"F3.imprint","IMPRINT",FACE,{"disambiguationData":[TD([[makeQuery(id+"F3.imprint","IMPRINT",EDGE,{"disambiguationData":[TD([[subQ6,1.0]])],"derivedFrom":subQ5}),-1.0]])]});}
            var Q3;
            {var subQ0=sQuery(id+"F3.wireOp",EDGE,"E48");var subQ1=sQuery(id+"F3.wireOp",EDGE,"E46");var subQ2=makeQuery(id+"F3.imprint","INTERSECT",VERTEX,{"disambiguationData":[OD(0.0)],"derivedFrom":[subQ1,subQ0]});Q3=makeQuery(id+"F3.imprint","IMPRINT",FACE,{"disambiguationData":[TD([[makeQuery(id+"F3.imprint","IMPRINT",EDGE,{"disambiguationData":[TD([[subQ2,1.0]])],"derivedFrom":subQ1}),-1.0]])]});}
            var Q4;
            {var subQ0=sQuery(id+"F3.wireOp",EDGE,"E49");var subQ1=sQuery(id+"F3.wireOp",EDGE,"E46");var subQ2=makeQuery(id+"F3.imprint","INTERSECT",VERTEX,{"derivedFrom":[subQ1,subQ0]});Q4=makeQuery(id+"F3.imprint","IMPRINT",FACE,{"disambiguationData":[TD([[makeQuery(id+"F3.imprint","IMPRINT",EDGE,{"disambiguationData":[TD([[subQ2,-1.0]])],"derivedFrom":subQ1}),1.0]])]});}
            extrude(context, id + "F7", {"entities" : qUnion([Q0, Q1, Q2, Q3, Q4]), "operationType" : NewBodyOperationType.ADD, "oppositeDirection" : true, "depth" : 25 * mm, "offsetDistance" : 25 * mm});
        }
        {
            var Q0;
            {var subQ0=sQuery(id+"F3.wireOp",EDGE,"E50");var subQ1=sQuery(id+"F3.wireOp",EDGE,"E49");var subQ2=makeQuery(id+"F3.imprint","INTERSECT",VERTEX,{"disambiguationData":[OD(0.0)],"derivedFrom":[subQ1,subQ0]});Q0=makeQuery(id+"F3.imprint","IMPRINT",FACE,{"disambiguationData":[TD([[makeQuery(id+"F3.imprint","IMPRINT",EDGE,{"disambiguationData":[TD([[subQ2,-1.0]])],"derivedFrom":subQ1}),-1.0]])]});}
            var Q1;
            {var subQ0=sQuery(id+"F3.wireOp",EDGE,"E50");var subQ1=sQuery(id+"F3.wireOp",EDGE,"E49");var subQ2=makeQuery(id+"F3.imprint","INTERSECT",VERTEX,{"disambiguationData":[OD(0.0)],"derivedFrom":[subQ1,subQ0]});Q1=makeQuery(id+"F3.imprint","IMPRINT",FACE,{"disambiguationData":[TD([[makeQuery(id+"F3.imprint","IMPRINT",EDGE,{"disambiguationData":[TD([[subQ2,-1.0]])],"derivedFrom":subQ1}),1.0]])]});}
            extrude(context, id + "F8", {"entities" : qUnion([Q0, Q1]), "operationType" : NewBodyOperationType.ADD, "depth" : 25 * mm, "offsetDistance" : 25 * mm, "hasSecondDirection" : true, "secondDirectionOppositeDirection" : true, "secondDirectionDepth" : 25 * mm});
        }
        {
            var Q0;
            Q0=makeQuery(id+"F3.imprint","IMPRINT",FACE,{"disambiguationData":[TD([[makeQuery(id+"F3.imprint","IMPRINT",EDGE,{"derivedFrom":sQuery(id+"F3.wireOp",EDGE,"E45")}),1.0]])]});
            extrude(context, id + "F9", {"entities" : qUnion([Q0]), "operationType" : NewBodyOperationType.ADD, "depth" : 50 * mm, "offsetDistance" : 25 * mm, "hasSecondDirection" : true, "secondDirectionOppositeDirection" : true, "secondDirectionDepth" : 50 * mm});
        }
    });
